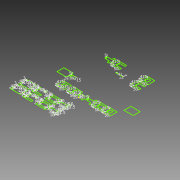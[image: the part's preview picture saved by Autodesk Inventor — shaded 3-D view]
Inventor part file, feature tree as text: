
AUTODESK INVENTOR PART (.ipt)
format: ipt  version: 2012 (Build 160160000, 160)  size: 210,432 bytes
history: native  units: mm
features: sketch x1
ambient origin geometry x8: Origin, YZ Plane, XZ Plane, XY Plane, X Axis, Y Axis, Z Axis, Center Point
feature tree (1):
  sketch  "Sketch1"  dims[d0=5.0mm d1=5.0mm d2=50.0mm d3=41.0mm d4=5.0mm d5=5.0mm d6=5.0mm d7=50.0mm d8=41.0mm d9=2.0mm d10=41.0mm d11=5.0mm d12=5.0mm d13=5.0mm d14=50.0mm d15=41.0mm d16=5.0mm d17=5.0mm d18=50.0mm d19=41.0mm d20=5.0mm d21=5.0mm d22=5.0mm d23=50.0mm d24=41.0mm d25=5.0mm d26=5.0mm d27=5.0mm d28=50.0mm d29=41.0mm d30=5.0mm d31=5.0mm d32=50.0mm d33=41.0mm d35=15.0mm d36=29.996525mm d41=21.0mm d42=15.0mm d43=29.996525mm d44=35.0mm d53=21.0mm d54=20.0mm d55=35.0mm d57=2.0mm d58=10.0mm d59=43.0mm d60=10.0mm d61=14.0mm d62=14.0mm d66=2.0mm d69=43.0mm d71=40.0mm d72=23.0mm d73=2.0mm d74=10.0mm d75=50.0mm d76=43.0mm d77=60.0mm d78=43.0mm d88=3.0mm d89=21.5mm d91=5.0mm d92=3.0mm d93=5.0mm d94=21.5mm d95=60.0mm d96=43.0mm d97=3.0mm d98=21.5mm d99=5.0mm d100=3.0mm d101=5.0mm d102=21.5mm d103=3.0mm d104=5.0mm d105=21.5mm d106=40.0mm d107=23.0mm d108=2.0mm d109=10.0mm d110=50.0mm d111=43.0mm d112=3.0mm d113=5.0mm d114=21.5mm d115=3.0mm d116=5.0mm d117=21.5mm d118=3.0mm d119=5.0mm d120=21.5mm d121=2.0mm d122=43.0mm d123=3.0mm d124=5.0mm d125=21.5mm d126=3.0mm d127=5.0mm d128=21.5mm d129=3.0mm d130=5.0mm d131=21.5mm d132=35.0mm d133=2.0mm d134=10.0mm d135=43.0mm d136=10.0mm d137=14.0mm d138=14.0mm d139=3.0mm d140=5.0mm d141=21.5mm]
